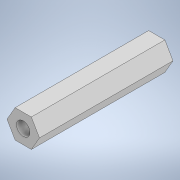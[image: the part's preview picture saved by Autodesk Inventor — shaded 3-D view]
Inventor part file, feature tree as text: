
AUTODESK INVENTOR PART (.ipt)
format: ipt  version: 2022.2 (Build 262287010, 287A)  size: 115,712 bytes
history: native  units: in
note: dims shown in document units (in); Inventor stores cm internally (conversion verified against a paired STEP export)
features: sketch x3, hole x2, extrude x1
ambient origin geometry x8: Origin, YZ Plane, XZ Plane, XY Plane, X Axis, Y Axis, Z Axis, Center Point
bodies: Body1 (feature_tree)
feature tree (6):
  extrude  "Extrusion2"  Depth=0.5in
  hole  "Hole1"  [1 undecoded]
  hole  "Hole2"  [1 undecoded]
  sketch  "Sketch1"  dims[d0=0.5in d3=0.159in]
  sketch  "Sketch2"  dims[d4=2.375in d5=0.0in]
  sketch  "Sketch3"  dims[d6=0.23in d7=0.75in d8=0.24in d9=0.2411in d10=0.5635in d11=0.31in d12=0.0in d13=0.23in d14=0.75in d15=0.24in d16=0.2411in d17=0.5635in d18=0.31in d19=0.0in]
note: 2 required parameter values undecoded (feature->parameter linkage not recoverable at this tier; creation-order binding heuristic only, values carry confidence <= 0.55)
